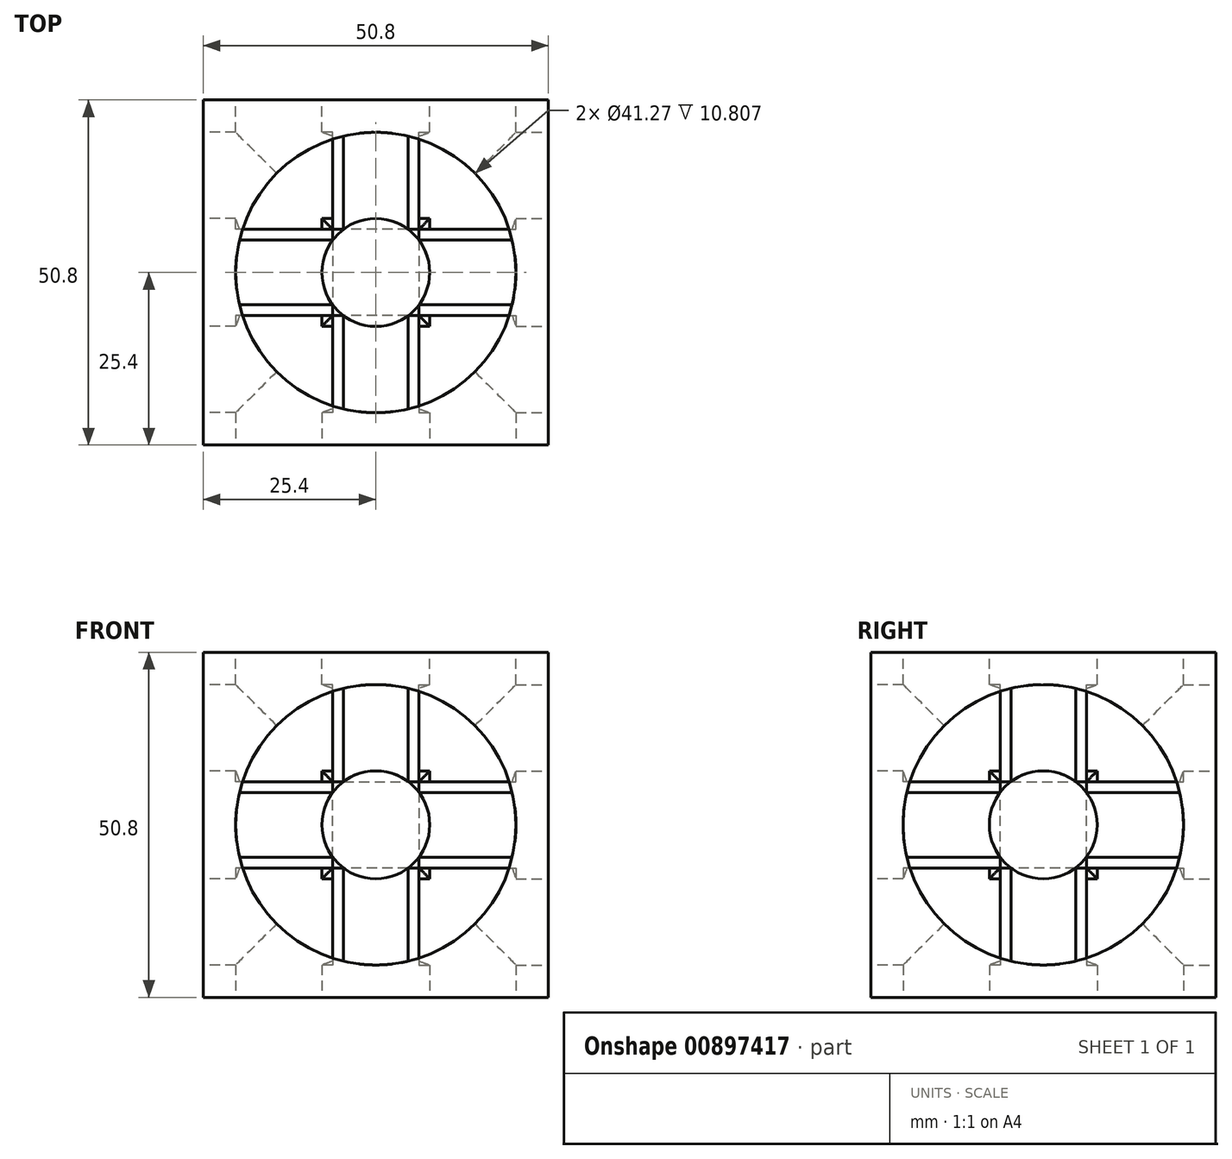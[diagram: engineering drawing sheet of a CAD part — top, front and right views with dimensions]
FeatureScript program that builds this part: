
annotation { "Feature Type Name" : "Feature", "Feature Type Description" : "" }
export const myFeature = defineFeature(function(context is Context, id is Id, definition is map)
    precondition{}
    {
        {
            var Q0;
            Q0=qCreatedBy(makeId("Front.planeOp"),FACE);
            var sketch = newSketch(context, id + "F0", { "sketchPlane" : qUnion([Q0])});
            skLineSegment(sketch, "E0.bottom", {"start": v(-25.4, 25.4) * mm, "end": v(25.4, 25.4) * mm});
            skLineSegment(sketch, "E0.top", {"start": v(-25.4, -25.4) * mm, "end": v(25.4, -25.4) * mm});
            skLineSegment(sketch, "E0.left", {"start": v(-25.4, 25.4) * mm, "end": v(-25.4, -25.4) * mm});
            skLineSegment(sketch, "E0.right", {"start": v(25.4, 25.4) * mm, "end": v(25.4, -25.4) * mm});
            skSolve(sketch);
        }
        {
            var Q0;
            Q0=makeQuery(id+"F0.imprint","IMPRINT",FACE,{"disambiguationData":[TD([[makeQuery(id+"F0.imprint","IMPRINT",EDGE,{"derivedFrom":sQuery(id+"F0.wireOp",EDGE,"E0.bottom")}),-1.0]])]});
            extrude(context, id + "F1", {"entities" : qUnion([Q0]), "endBound" : BoundingType.SYMMETRIC, "depth" : 50.8 * mm, "offsetDistance" : 25.4 * mm});
        }
        {
            var Q0;
            Q0=makeQuery(id+"F1.opExtrude","CAP_FACE",FACE,{"disambiguationData":[OSD([sQuery(id+"F0.wireOp",EDGE,"E0.bottom"),sQuery(id+"F0.wireOp",EDGE,"E0.top"),sQuery(id+"F0.wireOp",EDGE,"E0.left"),sQuery(id+"F0.wireOp",EDGE,"E0.right")])],"isStart":false});
            var sketch = newSketch(context, id + "F2", { "sketchPlane" : qUnion([Q0])});
            skCircle(sketch, "E1", {"center": v(0, 0) * mm, "radius": 20.64 * mm});
            skCircle(sketch, "E2", {"center": v(0, 0) * mm, "radius": 7.94 * mm});
            skSolve(sketch);
        }
        {
            var Q0;
            Q0=makeQuery(id+"F2.imprint","IMPRINT",FACE,{"disambiguationData":[TD([[makeQuery(id+"F2.imprint","IMPRINT",EDGE,{"derivedFrom":sQuery(id+"F2.wireOp",EDGE,"E1")}),1.0]])]});
            extrude(context, id + "F3", {"entities" : qUnion([Q0]), "operationType" : NewBodyOperationType.REMOVE, "oppositeDirection" : true, "depth" : 19.05 * mm, "offsetDistance" : 25.4 * mm});
        }
        {
            var Q0;
            Q0=makeQuery(id+"F1.opExtrude","SWEPT_FACE",FACE,{"disambiguationData":[OSD([sQuery(id+"F0.wireOp",EDGE,"E0.left")])]});
            var sketch = newSketch(context, id + "F4", { "sketchPlane" : qUnion([Q0])});
            skSolve(sketch);
        }
        {
            var Q0;
            Q0=makeQuery(id+"F1.opExtrude","SWEPT_FACE",FACE,{"disambiguationData":[OSD([sQuery(id+"F0.wireOp",EDGE,"E0.right")])]});
            var sketch = newSketch(context, id + "F5", { "sketchPlane" : qUnion([Q0])});
            skCircle(sketch, "E3", {"center": v(0, 0) * mm, "radius": 7.94 * mm});
            skCircle(sketch, "E4", {"center": v(0, 0) * mm, "radius": 20.64 * mm});
            skSolve(sketch);
        }
        {
            var Q0;
            Q0=makeQuery(id+"F5.imprint","IMPRINT",FACE,{"disambiguationData":[TD([[makeQuery(id+"F5.imprint","IMPRINT",EDGE,{"derivedFrom":sQuery(id+"F5.wireOp",EDGE,"E3")}),-1.0]])]});
            extrude(context, id + "F6", {"entities" : qUnion([Q0]), "operationType" : NewBodyOperationType.REMOVE, "oppositeDirection" : true, "depth" : 19.05 * mm, "offsetDistance" : 25.4 * mm});
        }
        {
            var Q0;
            Q0=makeQuery(id+"F1.opExtrude","SWEPT_FACE",FACE,{"disambiguationData":[OSD([sQuery(id+"F0.wireOp",EDGE,"E0.bottom")])]});
            var sketch = newSketch(context, id + "F7", { "sketchPlane" : qUnion([Q0])});
            skCircle(sketch, "E5", {"center": v(0, 0) * mm, "radius": 7.94 * mm});
            skCircle(sketch, "E6", {"center": v(0, 0) * mm, "radius": 20.64 * mm});
            skSolve(sketch);
        }
        {
            var Q0;
            Q0=makeQuery(id+"F7.imprint","IMPRINT",FACE,{"disambiguationData":[TD([[makeQuery(id+"F7.imprint","IMPRINT",EDGE,{"derivedFrom":sQuery(id+"F7.wireOp",EDGE,"E5")}),-1.0]])]});
            extrude(context, id + "F8", {"entities" : qUnion([Q0]), "operationType" : NewBodyOperationType.REMOVE, "oppositeDirection" : true, "depth" : 19.05 * mm, "offsetDistance" : 25.4 * mm});
        }
        {
            var Q0;
            Q0=makeQuery(id+"F1.opExtrude","SWEPT_FACE",FACE,{"disambiguationData":[OSD([sQuery(id+"F0.wireOp",EDGE,"E0.top")])]});
            var sketch = newSketch(context, id + "F9", { "sketchPlane" : qUnion([Q0])});
            skCircle(sketch, "E7", {"center": v(0, 0) * mm, "radius": 7.94 * mm});
            skCircle(sketch, "E8", {"center": v(0, 0) * mm, "radius": 20.64 * mm});
            skSolve(sketch);
        }
        {
            var Q0;
            Q0=makeQuery(id+"F9.imprint","IMPRINT",FACE,{"disambiguationData":[TD([[makeQuery(id+"F9.imprint","IMPRINT",EDGE,{"derivedFrom":sQuery(id+"F9.wireOp",EDGE,"E7")}),-1.0]])]});
            extrude(context, id + "F10", {"entities" : qUnion([Q0]), "operationType" : NewBodyOperationType.REMOVE, "oppositeDirection" : true, "depth" : 19.05 * mm, "offsetDistance" : 25.4 * mm});
        }
        {
            var Q0;
            {var subQ0=sQuery(id+"F0.wireOp",EDGE,"E0.left");Q0=makeQuery(id+"F4.imprint","IMPRINT",FACE,{"disambiguationData":[TD([[makeQuery(id+"F4.imprint","IMPRINT",EDGE,{"derivedFrom":makeQuery(id+"F1.opExtrude","CAP_EDGE",EDGE,{"disambiguationData":[OSD([subQ0])],"isStart":true})}),1.0]])]});}
            var sketch = newSketch(context, id + "F11", { "sketchPlane" : qUnion([Q0])});
            skSolve(sketch);
        }
        {
            var Q0;
            {var subQ0=sQuery(id+"F0.wireOp",EDGE,"E0.left");Q0=makeQuery(id+"F11.imprint","IMPRINT",FACE,{"disambiguationData":[TD([[makeQuery(id+"F11.imprint","IMPRINT",EDGE,{"derivedFrom":makeQuery(id+"F4.imprint","IMPRINT",EDGE,{"derivedFrom":makeQuery(id+"F1.opExtrude","CAP_EDGE",EDGE,{"disambiguationData":[OSD([subQ0])],"isStart":true})})}),1.0]])]});}
            var sketch = newSketch(context, id + "F12", { "sketchPlane" : qUnion([Q0])});
            skCircle(sketch, "E9", {"center": v(0, 0) * mm, "radius": 7.94 * mm});
            skCircle(sketch, "E10", {"center": v(0, 0) * mm, "radius": 20.64 * mm});
            skSolve(sketch);
        }
        {
            var Q0;
            Q0=makeQuery(id+"F12.imprint","IMPRINT",FACE,{"disambiguationData":[TD([[makeQuery(id+"F12.imprint","IMPRINT",EDGE,{"derivedFrom":sQuery(id+"F12.wireOp",EDGE,"E9")}),-1.0]])]});
            extrude(context, id + "F13", {"entities" : qUnion([Q0]), "operationType" : NewBodyOperationType.REMOVE, "oppositeDirection" : true, "depth" : 19.05 * mm, "offsetDistance" : 25.4 * mm});
        }
        {
            var Q0;
            Q0=makeQuery(id+"F1.opExtrude","CAP_FACE",FACE,{"disambiguationData":[OSD([sQuery(id+"F0.wireOp",EDGE,"E0.bottom"),sQuery(id+"F0.wireOp",EDGE,"E0.top"),sQuery(id+"F0.wireOp",EDGE,"E0.left"),sQuery(id+"F0.wireOp",EDGE,"E0.right")])],"isStart":true});
            var sketch = newSketch(context, id + "F14", { "sketchPlane" : qUnion([Q0])});
            skCircle(sketch, "E11", {"center": v(0, 0) * mm, "radius": 7.94 * mm});
            skCircle(sketch, "E12", {"center": v(0, 0) * mm, "radius": 20.64 * mm});
            skSolve(sketch);
        }
        {
            var Q0;
            Q0=makeQuery(id+"F14.imprint","IMPRINT",FACE,{"disambiguationData":[TD([[makeQuery(id+"F14.imprint","IMPRINT",EDGE,{"derivedFrom":sQuery(id+"F14.wireOp",EDGE,"E11")}),-1.0]])]});
            extrude(context, id + "F15", {"entities" : qUnion([Q0]), "operationType" : NewBodyOperationType.REMOVE, "oppositeDirection" : true, "depth" : 19.05 * mm, "offsetDistance" : 25.4 * mm});
        }
    });
